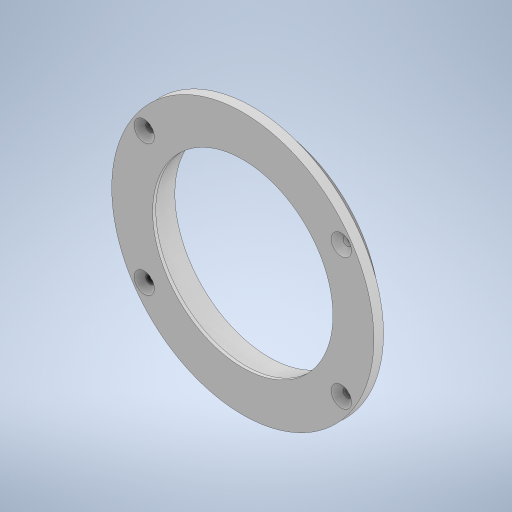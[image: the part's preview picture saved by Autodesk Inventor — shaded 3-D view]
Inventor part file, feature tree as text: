
AUTODESK INVENTOR PART (.ipt)
format: ipt  version: 2023.4 (Build 274418000, 418)  size: 368,640 bytes
history: native  units: mm
features: extrude x10, sketch x5, projected_geometry x2, chamfer x1
ambient origin geometry x8: Origin, YZ Plane, XZ Plane, XY Plane, X Axis, Y Axis, Z Axis, Center Point
bodies: Solid1 (feature_tree)
feature tree (18):
  extrude  "Extrusion1"  Depth=4.6mm
  extrude  "Extrusion2"  Depth=4.6mm
  extrude  "Extrusion3"  Depth=2.0mm TaperAngle=0.0deg
  extrude  "Extrusion4"  Depth=1.5mm TaperAngle=0.0deg
  extrude  "Extrusion7"  Depth=10.0mm
  extrude  "Extrusion10"  Depth=10.0mm
  chamfer  "Chamfer5"  Distance=4.0mm
  extrude  "Extrusion11"  Depth=10.0mm TaperAngle=0.0deg
  extrude  "Extrusion13"  Depth=2.0mm TaperAngle=45.0deg
  extrude  "Extrusion14"  TaperAngle=0.0deg  [1 undecoded]
  extrude  "Extrusion15"  Depth=10.0mm
  sketch  "Sketch1"  dims[d0=4.6mm d1=0.0mm d2=100.1mm]
  projected_geometry  "Projected Loop1"
  sketch  "Sketch12"  dims[d3=4.6mm d4=0.0mm d5=105.0mm]
  sketch  "Sketch14"  dims[d6=8.0mm d7=0.0mm d11=2.0mm d12=0.0mm]
  projected_geometry  "Projected Loop3"
  sketch  "Sketch15"  dims[d29=96.0mm d30=1.5mm d31=0.0mm]
  sketch  "Sketch16"  dims[d55=4.0mm d56=4.0mm d57=4.0mm d58=4.0mm d59=10.0mm d60=0.0mm d61=2.8mm d62=2.0mm d63=45.0deg d64=0.0mm d65=0.0mm d72=123.0mm d73=1.0mm d74=10.0mm d75=0.0mm d76=90.0mm d77=10.0mm d78=0.0mm d79=2.0mm d80=10.0mm d81=0.0mm]
note: 1 required parameter value undecoded (feature->parameter linkage not recoverable at this tier; creation-order binding heuristic only, values carry confidence <= 0.55)
